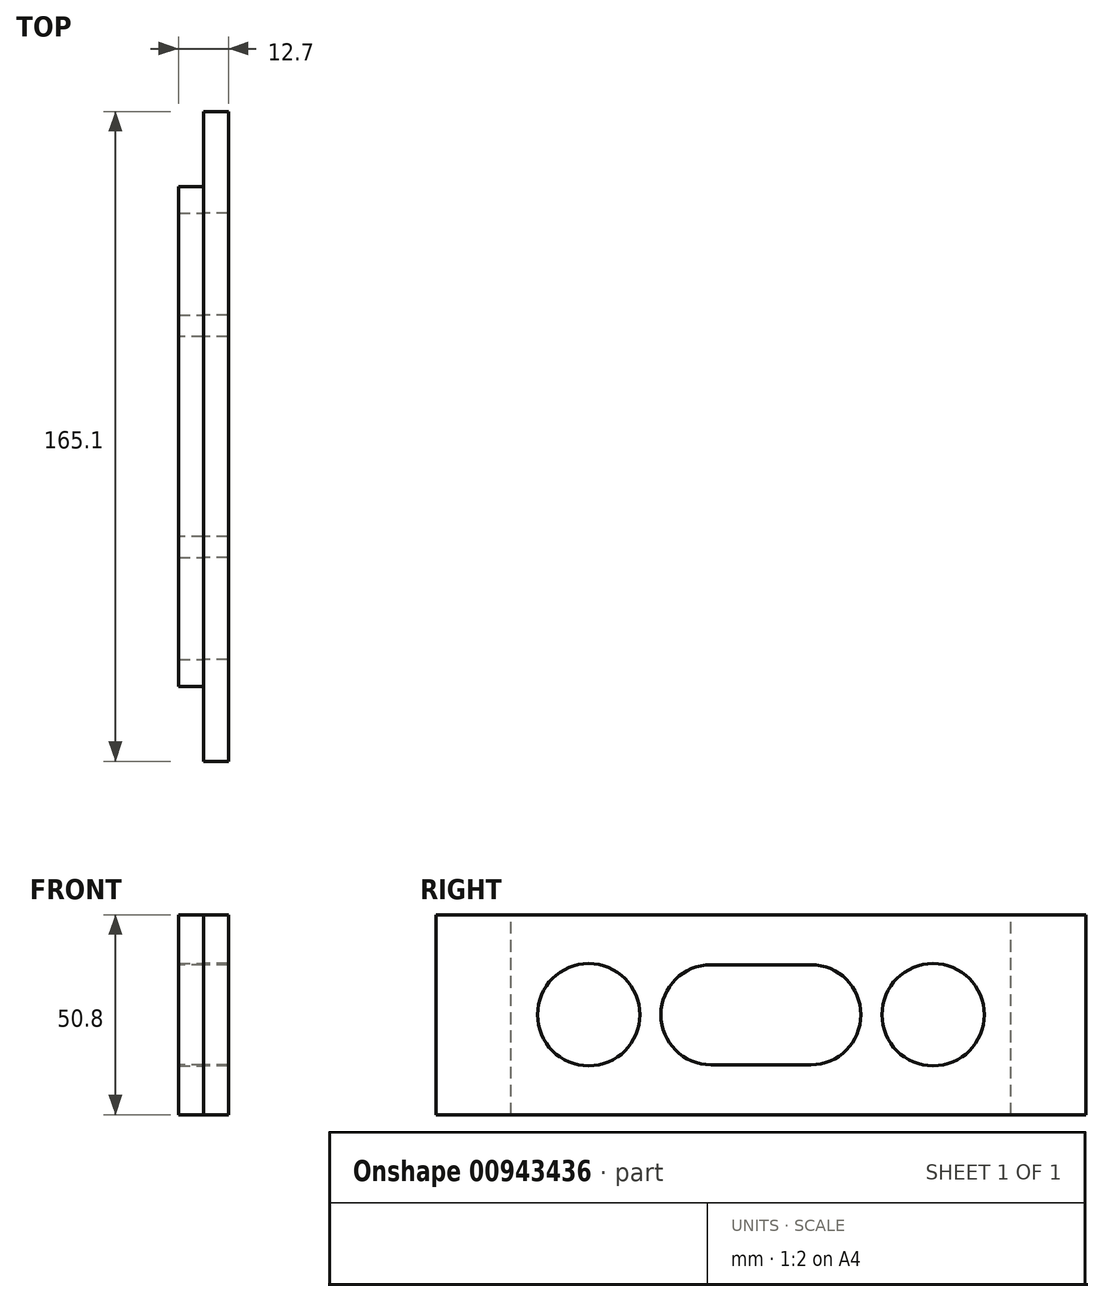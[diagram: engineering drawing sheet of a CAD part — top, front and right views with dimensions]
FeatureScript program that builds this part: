
annotation { "Feature Type Name" : "Feature", "Feature Type Description" : "" }
export const myFeature = defineFeature(function(context is Context, id is Id, definition is map)
    precondition{}
    {
        {
            var Q0;
            Q0=qCreatedBy(makeId("Right.planeOp"),FACE);
            var sketch = newSketch(context, id + "F0", { "sketchPlane" : qUnion([Q0])});
            skLineSegment(sketch, "E0.bottom", {"start": v(0, 0) * mm, "end": v(-165.1, 0) * mm});
            skLineSegment(sketch, "E0.top", {"start": v(0, 50.8) * mm, "end": v(-165.1, 50.8) * mm});
            skLineSegment(sketch, "E0.left", {"start": v(0, 0) * mm, "end": v(0, 50.8) * mm});
            skLineSegment(sketch, "E0.right", {"start": v(-165.1, 0) * mm, "end": v(-165.1, 50.8) * mm});
            skCircle(sketch, "E1", {"center": v(-126.3, 25.4) * mm, "radius": 13 * mm});
            skCircle(sketch, "E2", {"center": v(-38.8, 25.4) * mm, "radius": 13 * mm});
            skPoint(sketch, "E3", {"position": v(0, 25.4) * mm});
            skLineSegment(sketch, "E4", {"start": v(-126.3, 25.4) * mm, "end": v(-38.8, 25.4) * mm});
            skPoint(sketch, "E5", {"position": v(-82.55, 25.4) * mm});
            skPoint(sketch, "E6", {"position": v(-82.55, 50.8) * mm});
            skSolve(sketch);
        }
        {
            var Q0;
            Q0=makeQuery(id+"F0.imprint","IMPRINT",FACE,{"disambiguationData":[TD([[makeQuery(id+"F0.imprint","IMPRINT",EDGE,{"derivedFrom":sQuery(id+"F0.wireOp",EDGE,"E0.bottom")}),-1.0]])]});
            extrude(context, id + "F1", {"entities" : qUnion([Q0]), "depth" : 6.35 * mm, "offsetDistance" : 25.4 * mm});
        }
        {
            var Q0;
            Q0=makeQuery(id+"F1.opExtrude","CAP_FACE",FACE,{"disambiguationData":[OSD([sQuery(id+"F0.wireOp",EDGE,"E0.bottom"),sQuery(id+"F0.wireOp",EDGE,"E0.top"),sQuery(id+"F0.wireOp",EDGE,"E0.left"),sQuery(id+"F0.wireOp",EDGE,"E0.right"),sQuery(id+"F0.wireOp",EDGE,"E1"),sQuery(id+"F0.wireOp",EDGE,"E2")])],"isStart":true});
            var sketch = newSketch(context, id + "F2", { "sketchPlane" : qUnion([Q0])});
            skLineSegment(sketch, "E7.0.0", {"start": v(0, 50.8) * mm, "end": v(0, 0) * mm});
            skLineSegment(sketch, "E7.0.1", {"start": v(0, 0) * mm, "end": v(165.1, 0) * mm});
            skLineSegment(sketch, "E7.0.2", {"start": v(165.1, 0) * mm, "end": v(165.1, 50.8) * mm});
            skLineSegment(sketch, "E7.0.3", {"start": v(165.1, 50.8) * mm, "end": v(0, 50.8) * mm});
            skLineSegment(sketch, "E8.bottom", {"start": v(19.05, 0) * mm, "end": v(146.05, 0) * mm});
            skLineSegment(sketch, "E8.top", {"start": v(19.05, 50.8) * mm, "end": v(146.05, 50.8) * mm});
            skLineSegment(sketch, "E8.left", {"start": v(19.05, 0) * mm, "end": v(19.05, 50.8) * mm});
            skLineSegment(sketch, "E8.right", {"start": v(146.05, 0) * mm, "end": v(146.05, 50.8) * mm});
            skPoint(sketch, "E9", {"position": v(82.55, 50.8) * mm});
            skSolve(sketch);
        }
        {
            var Q0;
            {var subQ1=sQuery(id+"F2.wireOp",EDGE,"E8.left");Q0=makeQuery(id+"F2.imprint","IMPRINT",FACE,{"disambiguationData":[TD([[makeQuery(id+"F2.imprint","IMPRINT",EDGE,{"derivedFrom":subQ1}),-1.0]])]});}
            extrude(context, id + "F3", {"entities" : qUnion([Q0]), "depth" : 6.35 * mm, "offsetDistance" : 25.4 * mm});
        }
        {
            var Q0;
            Q0=makeQuery(id+"F3.opExtrude","CAP_FACE",FACE,{"disambiguationData":[OSD([sQuery(id+"F0.wireOp",EDGE,"E1"),sQuery(id+"F0.wireOp",EDGE,"E2"),sQuery(id+"F2.wireOp",EDGE,"E7.0.1"),sQuery(id+"F2.wireOp",EDGE,"E7.0.3"),sQuery(id+"F2.wireOp",EDGE,"E8.left"),sQuery(id+"F2.wireOp",EDGE,"E8.right")])],"isStart":false});
            var sketch = newSketch(context, id + "F4", { "sketchPlane" : qUnion([Q0])});
            skCircle(sketch, "E10", {"center": v(69.85, 25.4) * mm, "radius": 12.7 * mm});
            skCircle(sketch, "E11", {"center": v(95.25, 25.4) * mm, "radius": 12.7 * mm});
            skPoint(sketch, "E12", {"position": v(146.05, 25.4) * mm});
            skLineSegment(sketch, "E13", {"start": v(69.85, 25.4) * mm, "end": v(95.25, 25.4) * mm});
            skPoint(sketch, "E14", {"position": v(82.55, 50.8) * mm});
            skPoint(sketch, "E15", {"position": v(82.55, 25.4) * mm});
            skLineSegment(sketch, "E16", {"start": v(95.25, 38.1) * mm, "end": v(69.85, 38.1) * mm});
            skLineSegment(sketch, "E17", {"start": v(69.85, 12.7) * mm, "end": v(95.25, 12.7) * mm});
            skSolve(sketch);
        }
        {
            var Q0;
            Q0 = qSketchRegion(id + "F4", true);
            extrude(context, id + "F5", {"entities" : qUnion([Q0]), "operationType" : NewBodyOperationType.REMOVE, "endBound" : BoundingType.THROUGH_ALL, "oppositeDirection" : true, "depth" : 25.4 * mm, "offsetDistance" : 25.4 * mm});
        }
    });
